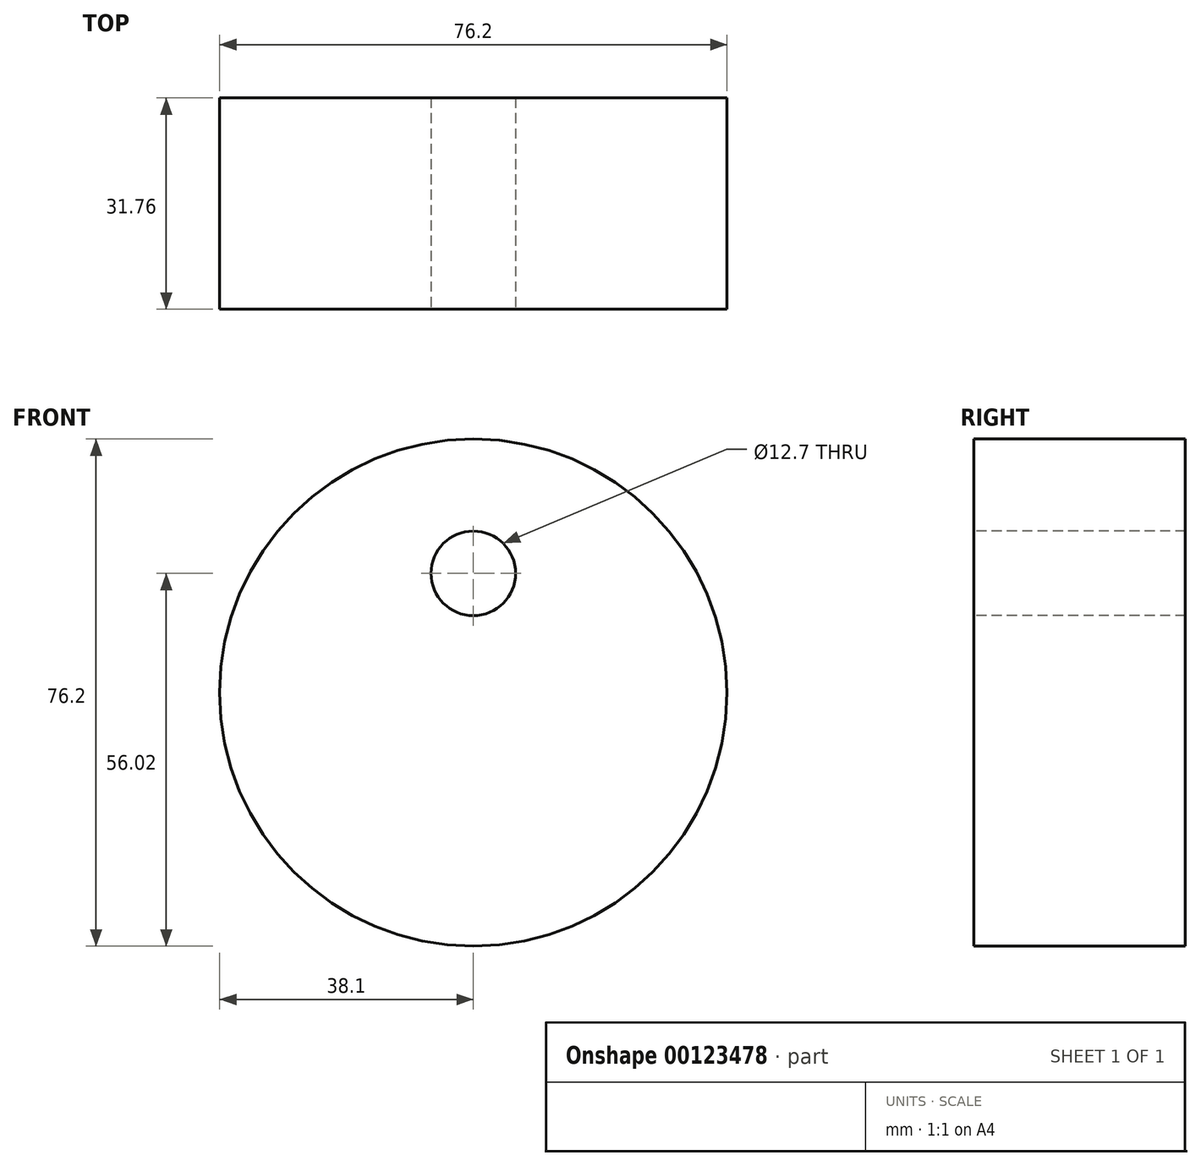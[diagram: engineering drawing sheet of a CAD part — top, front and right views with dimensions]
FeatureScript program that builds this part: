
annotation { "Feature Type Name" : "Feature", "Feature Type Description" : "" }
export const myFeature = defineFeature(function(context is Context, id is Id, definition is map)
    precondition{}
    {
        {
            var Q0;
            Q0=qCreatedBy(makeId("Front.planeOp"),FACE);
            var sketch = newSketch(context, id + "F0", { "sketchPlane" : qUnion([Q0])});
            skCircle(sketch, "E0", {"center": v(0, 0) * mm, "radius": 38.1 * mm});
            skSolve(sketch);
        }
        {
            var Q0;
            Q0=qSketchRegion(id+"F0",true);
            extrude(context, id + "F1", {"entities" : qUnion([Q0]), "endBound" : BoundingType.SYMMETRIC, "depth" : 31.75 * mm});
        }
        {
            var Q0;
            Q0=qCreatedBy(makeId("Front.planeOp"),FACE);
            var sketch = newSketch(context, id + "F2", { "sketchPlane" : qUnion([Q0])});
            skCircle(sketch, "E1", {"center": v(0, 17.92) * mm, "radius": 6.35 * mm});
            skSolve(sketch);
        }
        {
            var Q0;
            Q0=qSketchRegion(id+"F2",true);
            extrude(context, id + "F3", {"entities" : qUnion([Q0]), "operationType" : NewBodyOperationType.REMOVE, "endBound" : BoundingType.SYMMETRIC, "oppositeDirection" : true, "depth" : 31.75 * mm});
        }
    });
